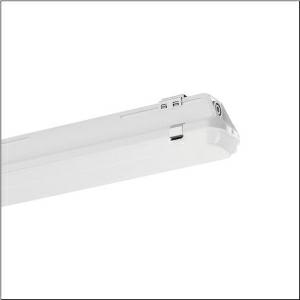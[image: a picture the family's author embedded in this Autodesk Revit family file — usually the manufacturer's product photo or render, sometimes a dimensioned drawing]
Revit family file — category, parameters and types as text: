
# Revit family: monsun_r__21_51fb10dp430b_6f0c
name_source: partatom
category: Lighting Fixtures
units: mm (PartAtom-declared; Revit-internal decimal feet)

## family parameters
Cut with Voids When Loaded = No
Host = Face
Light Source = No
Part Type = Normal
Room Calculation Point = No
Round Connector Dimension = Use Diameter
Shared = No

## types (1)
- --- (1 x LED, 3860 lm, 24.7 W, 4000K)
    Apparent Load = 25 VA
    CIE Flux Codes = 47 77 93 94 100
    Color Rendering = 80
    Color Temperature = 4000K
    Default Elevation = 1800 mm
    Description = Monsun® 21, damp-proof luminaire, chain hanger, primary optical cover: enclosure, of PMMA, light emission: direct distribution, primary light characteristic: symmetric, installation type: suspended mounting, surface-mounted, horizontal mounting, vertical mounting, LED, rated luminous flux: 3.860lm, luminous efficacy: 156lm/W, light colour: 840, colour temperature: 4000K, control gear: DALI 2, with terminal, 5-pole, max. 2.5mm², mains connection: 220..240V, AC, 50/60Hz, rated input power: 25W, housing, of glass-fibre reinforced polyester, uncoated, bright grey, incl. chain hanger, length: 1.590mm, width: 90mm, height: 88mm, clip for enclosure, of stainless steel (V2A), ceiling mounting element, of stainless steel (V2A), chain hanger, of stainless steel (V2A), protection rating (complete): IP66, insulation class (complete): insulation class I (protective earthing), certification: CE, ENEC, VDE, UKCA, protection symbol: D, impact resistance: IK04, permissible operating ambient temperature: -25..+35°C, standard: EN 50419, EN 60598-2-1, corresponds to IFS (International Featured Standards) requirements for safety and quality in the food industry, for indoor or canopied outdoor use, no direct snow, no direct sun, no direct rain, contact your sales advisor before using the luminaires in applications with unclear chemical exposure, large temperature fluctuations or condensation-forming humidity, LABS conformity tested according to VDMA 24364:2018-05, packaging unit: 1 piece
    Height = 89 mm
    Lamp = 1 x LED
    Lamp Light Flux = 3860 lm
    Lamp Power = 24.7 W
    Lamp count = 1
    Length = 1590 mm
    Luminous efficacy = 156 lm/W
    Manufacturer = Siteco
    ModVariant = No
    Model = 51FB10DP430B
    Mounting Place = Ceiling
    Mounting Type = Surface mounted
    Number of Poles = 1
    OnlyDefault = Yes
    Power Factor = 1
    Product Name = Monsun® 21
    Product group = damp-proof luminaire
    ProductGroupID = 300
    Protection Class = Protection class I
    Protection Degree = IP 66
    RLX_Detail_Level = 1
    RLX_Emergency_Light_Flux = 0 lm
    RLX_Emergency_Type = 0
    RLX_Emergency_Type_DB = No
    RlxData = <blob elided: 92101 chars, md5=f424db8a>
    Socket = socket
    Standby Power = 0 W
    System Light Flux = 3860 lm
    System Power = 25 W
    Type Comments = factory setting: luminous flux: 100 % | dim-lin: 254 | 162 mA
    Type Image = l_1319656.jpg
    URL = http://relux.com
    VarID = @adj_197342
    Voltage = 0 V
    Weight = 0.00 kg
    Width = 90 mm

## geometry (parser evidence)
native form markers: Blend x4, Sweep x14
no freeform markers — native parametric forms only
